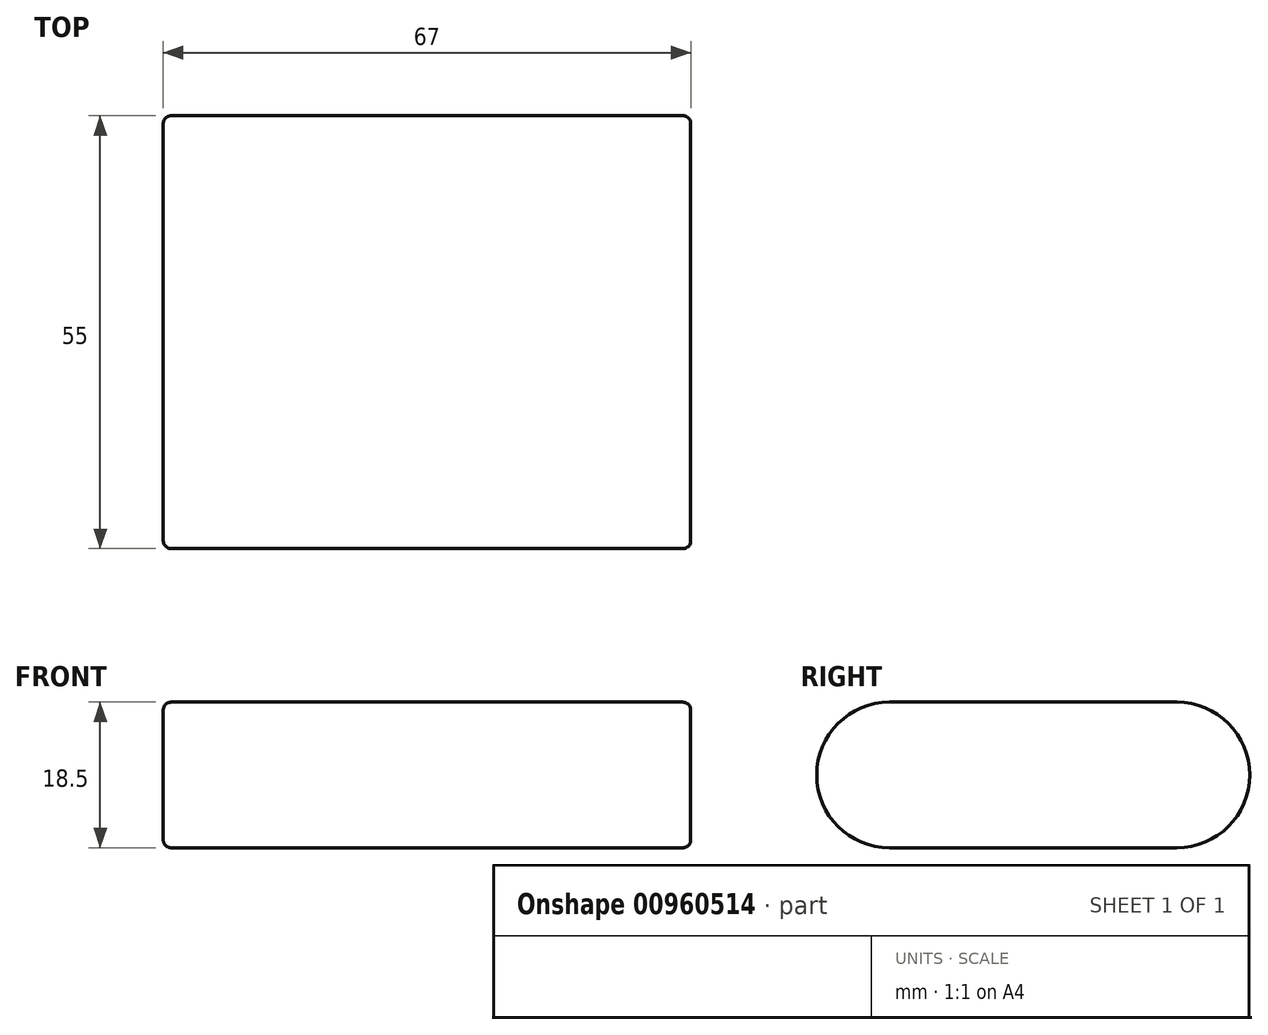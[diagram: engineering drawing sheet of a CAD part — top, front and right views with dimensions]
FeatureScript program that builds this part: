
annotation { "Feature Type Name" : "Feature", "Feature Type Description" : "" }
export const myFeature = defineFeature(function(context is Context, id is Id, definition is map)
    precondition{}
    {
        {
            assignVariable(context, id + "F0", {"name" : "THICKNESS", "anyValue" : 18.5});
        }
        {
            var Q0;
            Q0=qCreatedBy(makeId("Top.planeOp"),FACE);
            var sketch = newSketch(context, id + "F1", { "sketchPlane" : qUnion([Q0])});
            skLineSegment(sketch, "E0.bottom", {"start": v(-46.95, 17.2) * mm, "end": v(20.05, 17.2) * mm});
            skLineSegment(sketch, "E0.top", {"start": v(-46.95, -37.8) * mm, "end": v(20.05, -37.8) * mm});
            skLineSegment(sketch, "E0.left", {"start": v(-46.95, 17.2) * mm, "end": v(-46.95, -37.8) * mm});
            skLineSegment(sketch, "E0.right", {"start": v(20.05, 17.2) * mm, "end": v(20.05, -37.8) * mm});
            skSolve(sketch);
        }
        {
            var Q0;
            Q0=qSketchRegion(id+"F1",true);
            extrude(context, id + "F2", {"entities" : qUnion([Q0]), "depth" : (getVariable(context, 'THICKNESS')) * mm});
        }
        {
            var Q0;
            Q0=makeQuery(id+"F2.opExtrude","CAP_EDGE",EDGE,{"disambiguationData":[OSD([sQuery(id+"F1.wireOp",EDGE,"E0.bottom")])],"isStart":false});
            var Q1;
            Q1=makeQuery(id+"F2.opExtrude","CAP_EDGE",EDGE,{"disambiguationData":[OSD([sQuery(id+"F1.wireOp",EDGE,"E0.bottom")])],"isStart":true});
            var Q2;
            Q2=makeQuery(id+"F2.opExtrude","CAP_EDGE",EDGE,{"disambiguationData":[OSD([sQuery(id+"F1.wireOp",EDGE,"E0.top")])],"isStart":false});
            var Q3;
            Q3=makeQuery(id+"F2.opExtrude","CAP_EDGE",EDGE,{"disambiguationData":[OSD([sQuery(id+"F1.wireOp",EDGE,"E0.top")])],"isStart":true});
            fillet(context, id + "F3", {"entities" : qUnion([Q0, Q1, Q2, Q3]), "radius" : (getVariable(context, 'THICKNESS') / 2) * mm, "tangentPropagation" : true, "allowEdgeOverflow" : false});
        }
        {
            var Q0;
            Q0=makeQuery(id+"F2.opExtrude","SWEPT_FACE",FACE,{"disambiguationData":[OSD([sQuery(id+"F1.wireOp",EDGE,"E0.right")])]});
            var Q1;
            Q1=makeQuery(id+"F2.opExtrude","SWEPT_FACE",FACE,{"disambiguationData":[OSD([sQuery(id+"F1.wireOp",EDGE,"E0.left")])]});
            fillet(context, id + "F4", {"entities" : qUnion([Q0, Q1]), "radius" : 1 * mm, "tangentPropagation" : true, "allowEdgeOverflow" : false});
        }
    });
